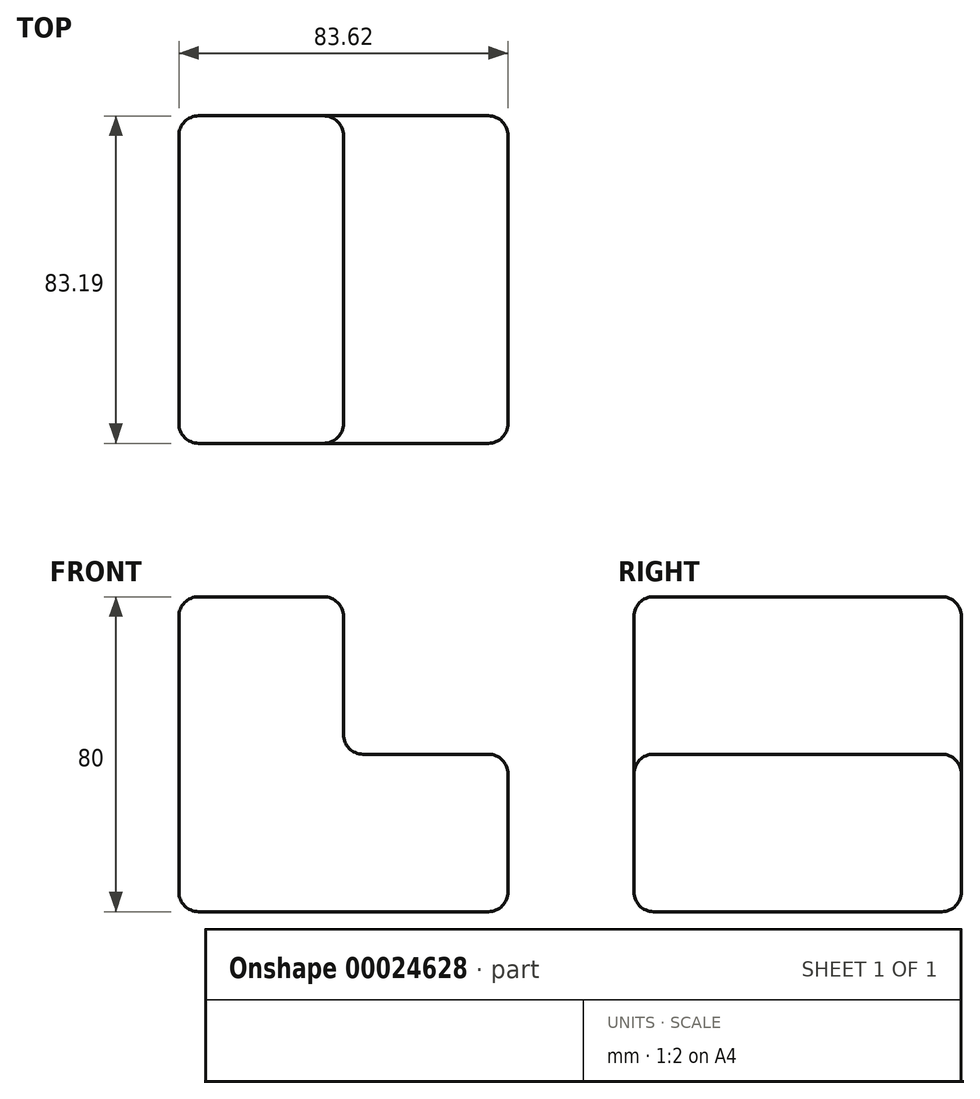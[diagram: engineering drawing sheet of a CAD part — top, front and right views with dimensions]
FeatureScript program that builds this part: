
annotation { "Feature Type Name" : "Feature", "Feature Type Description" : "" }
export const myFeature = defineFeature(function(context is Context, id is Id, definition is map)
    precondition{}
    {
        {
            var Q0;
            Q0=qCreatedBy(makeId("Top.planeOp"),FACE);
            var sketch = newSketch(context, id + "F0", { "sketchPlane" : qUnion([Q0])});
            skLineSegment(sketch, "E0.bottom", {"start": v(-59.13, -45.93) * mm, "end": v(24.5, -45.93) * mm});
            skLineSegment(sketch, "E0.top", {"start": v(-59.13, 37.26) * mm, "end": v(24.5, 37.26) * mm});
            skLineSegment(sketch, "E0.left", {"start": v(-59.13, -45.93) * mm, "end": v(-59.13, 37.26) * mm});
            skLineSegment(sketch, "E0.right", {"start": v(24.5, -45.93) * mm, "end": v(24.5, 37.26) * mm});
            skSolve(sketch);
        }
        {
            var Q0;
            Q0=makeQuery(id+"F0.imprint","IMPRINT",FACE,{"disambiguationData":[TD([[makeQuery(id+"F0.imprint","IMPRINT",EDGE,{"derivedFrom":sQuery(id+"F0.wireOp",EDGE,"E0.bottom")}),1.0]])]});
            extrude(context, id + "F1", {"entities" : qUnion([Q0]), "depth" : 40 * mm});
        }
        {
            var Q0;
            Q0=makeQuery(id+"F1.opExtrude","CAP_FACE",FACE,{"disambiguationData":[OSD([sQuery(id+"F0.wireOp",EDGE,"E0.bottom"),sQuery(id+"F0.wireOp",EDGE,"E0.top"),sQuery(id+"F0.wireOp",EDGE,"E0.left"),sQuery(id+"F0.wireOp",EDGE,"E0.right")])],"isStart":false});
            var sketch = newSketch(context, id + "F2", { "sketchPlane" : qUnion([Q0])});
            skLineSegment(sketch, "E1", {"start": v(-17.32, 37.26) * mm, "end": v(-17.32, -45.93) * mm});
            skSolve(sketch);
        }
        {
            var Q0;
            {var subQ1=sQuery(id+"F2.wireOp",EDGE,"E1");Q0=makeQuery(id+"F2.imprint","IMPRINT",FACE,{"disambiguationData":[TD([[makeQuery(id+"F2.imprint","IMPRINT",EDGE,{"derivedFrom":subQ1}),-1.0]])]});}
            extrude(context, id + "F3", {"entities" : qUnion([Q0]), "operationType" : NewBodyOperationType.ADD, "depth" : 40 * mm});
        }
        {
            var Q0;
            Q0=makeQuery(id+"F3.opExtrude","CAP_EDGE",EDGE,{"disambiguationData":[OSD([sQuery(id+"F0.wireOp",EDGE,"E0.bottom")])],"isStart":false});
            var Q1;
            Q1=makeQuery(id+"F1.opExtrude","CAP_EDGE",EDGE,{"disambiguationData":[OSD([sQuery(id+"F0.wireOp",EDGE,"E0.right")])],"isStart":false});
            var Q2;
            Q2=makeQuery(id+"F1.opExtrude","SWEPT_FACE",FACE,{"disambiguationData":[OSD([sQuery(id+"F0.wireOp",EDGE,"E0.right")])]});
            var Q3;
            Q3=makeQuery(id+"F3.opExtrude","CAP_EDGE",EDGE,{"disambiguationData":[OSD([sQuery(id+"F2.wireOp",EDGE,"E1")])],"isStart":true});
            var Q4;
            Q4=makeQuery(id+"F1.opExtrude","CAP_FACE",FACE,{"disambiguationData":[OSD([sQuery(id+"F0.wireOp",EDGE,"E0.bottom"),sQuery(id+"F0.wireOp",EDGE,"E0.top"),sQuery(id+"F0.wireOp",EDGE,"E0.left"),sQuery(id+"F0.wireOp",EDGE,"E0.right")])],"isStart":false});
            var Q5;
            Q5=makeQuery(id+"F3.opExtrude","CAP_EDGE",EDGE,{"disambiguationData":[OSD([sQuery(id+"F2.wireOp",EDGE,"E1")])],"isStart":false});
            var Q6;
            Q6=makeQuery(id+"F3.opExtrude","SWEPT_FACE",FACE,{"disambiguationData":[OSD([sQuery(id+"F2.wireOp",EDGE,"E1")])]});
            var Q7;
            Q7=makeQuery(id+"F1.opExtrude","CAP_EDGE",EDGE,{"disambiguationData":[OSD([sQuery(id+"F0.wireOp",EDGE,"E0.top")])],"isStart":true});
            var Q8;
            {var subQ0=sQuery(id+"F0.wireOp",EDGE,"E0.top");Q8=makeQuery(id+"F3.boolean.opBoolean","MERGE",FACE,{"derivedFrom":[makeQuery(id+"F1.opExtrude","SWEPT_FACE",FACE,{"disambiguationData":[OSD([subQ0])]}),makeQuery(id+"F3.opExtrude","SWEPT_FACE",FACE,{"disambiguationData":[OSD([subQ0])]})]});}
            var Q9;
            Q9=makeQuery(id+"F3.opExtrude","CAP_EDGE",EDGE,{"disambiguationData":[OSD([sQuery(id+"F0.wireOp",EDGE,"E0.top")])],"isStart":false});
            var Q10;
            Q10=makeQuery(id+"F1.opExtrude","CAP_EDGE",EDGE,{"disambiguationData":[OSD([sQuery(id+"F0.wireOp",EDGE,"E0.bottom")])],"isStart":true});
            var Q11;
            Q11=makeQuery(id+"F3.opExtrude","CAP_EDGE",EDGE,{"disambiguationData":[OSD([sQuery(id+"F0.wireOp",EDGE,"E0.left")])],"isStart":false});
            var Q12;
            Q12=makeQuery(id+"F1.opExtrude","CAP_EDGE",EDGE,{"disambiguationData":[OSD([sQuery(id+"F0.wireOp",EDGE,"E0.left")])],"isStart":true});
            fillet(context, id + "F4", {"entities" : qUnion([Q0, Q1, Q2, Q3, Q4, Q5, Q6, Q7, Q8, Q9, Q10, Q11, Q12]), "radius" : 5 * mm, "tangentPropagation" : true, "allowEdgeOverflow" : false});
        }
        {
            var Q0;
            {var subQ0=sQuery(id+"F0.wireOp",EDGE,"E0.bottom");var subQ1=sQuery(id+"F0.wireOp",EDGE,"E0.left");Q0=makeQuery(id+"F3.boolean.opBoolean","MERGE",EDGE,{"derivedFrom":[makeQuery(id+"F1.opExtrude","SWEPT_EDGE",EDGE,{"disambiguationData":[OSD([subQ0,subQ1])]}),makeQuery(id+"F3.opExtrude","SWEPT_EDGE",EDGE,{"disambiguationData":[OSD([subQ0,subQ1])]})]});}
            var Q1;
            {var subQ0=sQuery(id+"F0.wireOp",EDGE,"E0.left");Q1=makeQuery(id+"F3.boolean.opBoolean","MERGE",FACE,{"derivedFrom":[makeQuery(id+"F1.opExtrude","SWEPT_FACE",FACE,{"disambiguationData":[OSD([subQ0])]}),makeQuery(id+"F3.opExtrude","SWEPT_FACE",FACE,{"disambiguationData":[OSD([subQ0])]})]});}
            fillet(context, id + "F5", {"entities" : qUnion([Q0, Q1]), "radius" : 5 * mm, "tangentPropagation" : true, "allowEdgeOverflow" : false});
        }
    });
